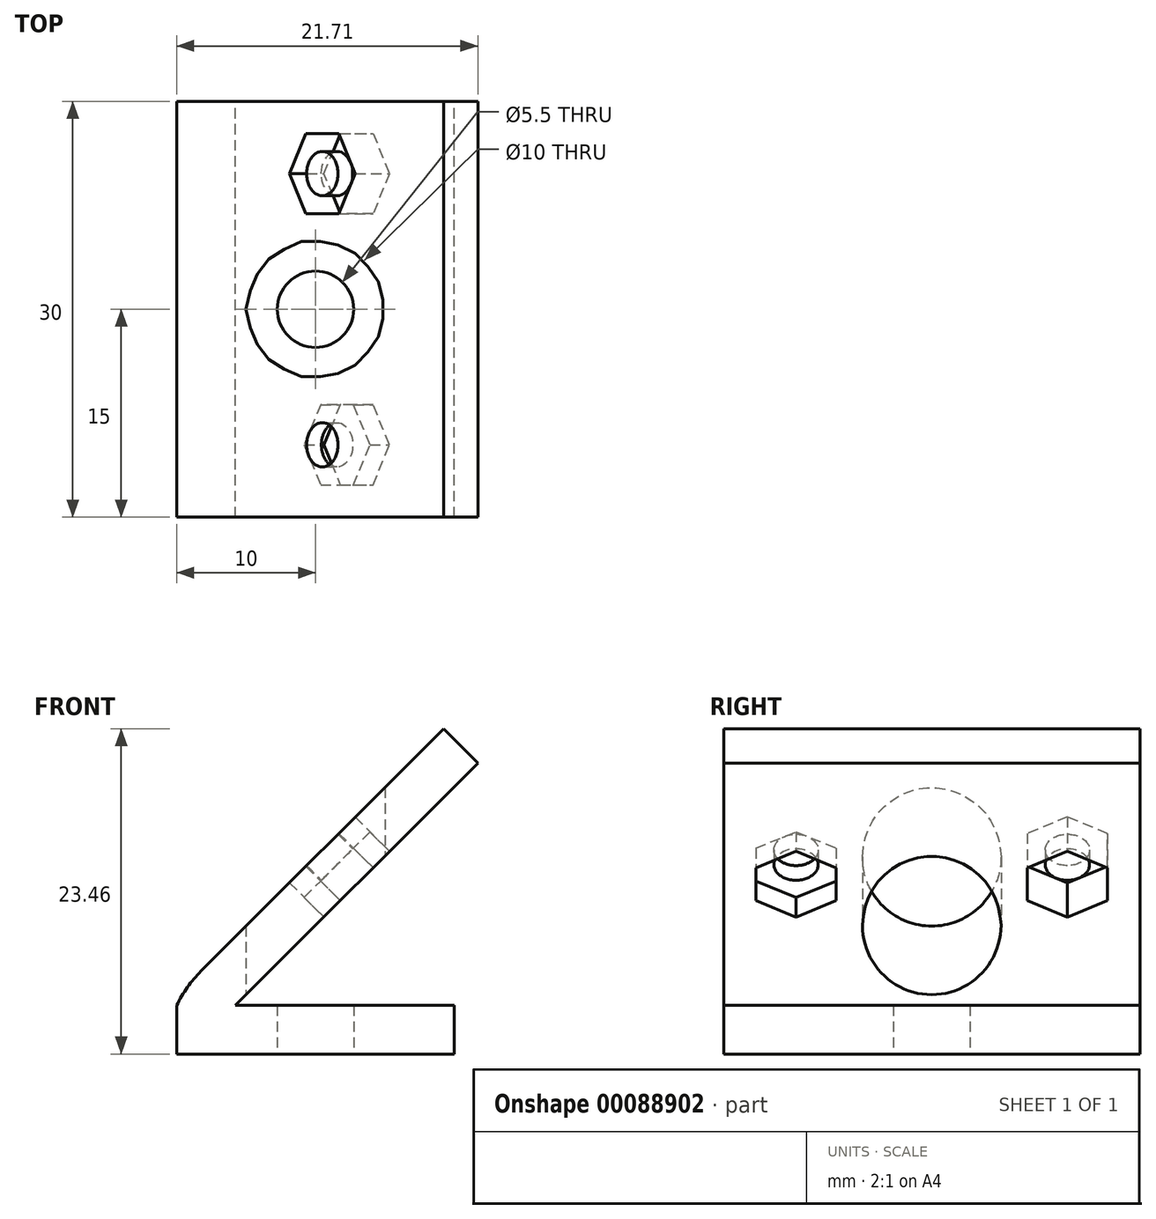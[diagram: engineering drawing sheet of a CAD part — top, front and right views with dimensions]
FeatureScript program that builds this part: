
annotation { "Feature Type Name" : "Feature", "Feature Type Description" : "" }
export const myFeature = defineFeature(function(context is Context, id is Id, definition is map)
    precondition{}
    {
        {
            var Q0;
            Q0=qCreatedBy(makeId("Front.planeOp"),FACE);
            var sketch = newSketch(context, id + "F0", { "sketchPlane" : qUnion([Q0])});
            skLineSegment(sketch, "E0.bottom", {"start": v(0, 0) * mm, "end": v(20, 0) * mm});
            skLineSegment(sketch, "E0.top", {"start": v(0, 3.5) * mm, "end": v(20, 3.5) * mm});
            skLineSegment(sketch, "E0.left", {"start": v(0, 0) * mm, "end": v(0, 3.5) * mm});
            skLineSegment(sketch, "E0.right", {"start": v(20, 0) * mm, "end": v(20, 3.5) * mm});
            skLineSegment(sketch, "E1", {"start": v(-13.12, -11.37) * mm, "end": v(33.48, 35.23) * mm, "construction": true});
            skPoint(sketch, "E2", {"position": v(0, 1.75) * mm});
            skLineSegment(sketch, "E3", {"start": v(-7.12, 1.75) * mm, "end": v(23.4, 1.75) * mm, "construction": true});
            skLineSegment(sketch, "E4", {"start": v(1.75, 5.97) * mm, "end": v(19.24, 23.46) * mm});
            skLineSegment(sketch, "E5", {"start": v(19.24, 23.46) * mm, "end": v(21.71, 20.99) * mm});
            skLineSegment(sketch, "E6", {"start": v(21.71, 20.99) * mm, "end": v(4.22, 3.5) * mm});
            skLineSegment(sketch, "E7", {"start": v(4.22, 3.5) * mm, "end": v(1.75, 5.97) * mm});
            skArc(sketch, "E8", {"start": v(1.75, 5.97) * mm, "mid": v(0.77, 4.81) * mm, "end": v(0, 3.5) * mm});
            skSolve(sketch);
        }
        {
            var Q0;
            Q0 = qSketchRegion(id + "F0", true);
            extrude(context, id + "F1", {"entities" : qUnion([Q0]), "depth" : 30 * mm});
        }
        {
            var Q0;
            Q0=makeQuery(id+"F1.opExtrude","SWEPT_FACE",FACE,{"disambiguationData":[OSD([sQuery(id+"F0.wireOp",EDGE,"E0.bottom")])]});
            var sketch = newSketch(context, id + "F2", { "sketchPlane" : qUnion([Q0])});
            skLineSegment(sketch, "E9", {"start": v(10, 34.29) * mm, "end": v(10, -9.4) * mm, "construction": true});
            skLineSegment(sketch, "E10", {"start": v(-12.53, 15) * mm, "end": v(35.25, 15) * mm, "construction": true});
            skCircle(sketch, "E11", {"center": v(10, 15) * mm, "radius": 2.75 * mm});
            skSolve(sketch);
        }
        {
            var Q0;
            Q0 = qSketchRegion(id + "F2", true);
            extrude(context, id + "F3", {"entities" : qUnion([Q0]), "operationType" : NewBodyOperationType.REMOVE, "endBound" : BoundingType.UP_TO_NEXT, "oppositeDirection" : true, "depth" : 25 * mm});
        }
        {
            var Q0;
            Q0=makeQuery(id+"F1.opExtrude","SWEPT_FACE",FACE,{"disambiguationData":[OSD([sQuery(id+"F0.wireOp",EDGE,"E0.top")])]});
            var sketch = newSketch(context, id + "F4", { "sketchPlane" : qUnion([Q0])});
            skCircle(sketch, "E12", {"center": v(10, -15) * mm, "radius": 5 * mm});
            skSolve(sketch);
        }
        {
            var Q0;
            Q0 = qSketchRegion(id + "F4", true);
            var Q1;
            Q1=makeQuery(id+"F1.opExtrude","SWEPT_FACE",FACE,{"disambiguationData":[OSD([sQuery(id+"F0.wireOp",EDGE,"E4")])]});
            extrude(context, id + "F5", {"entities" : qUnion([Q0]), "operationType" : NewBodyOperationType.REMOVE, "endBound" : BoundingType.UP_TO_SURFACE, "endBoundEntityFace" : qUnion([Q1]), "depth" : 25 * mm});
        }
        {
            var Q0;
            Q0=makeQuery(id+"F1.opExtrude","SWEPT_FACE",FACE,{"disambiguationData":[OSD([sQuery(id+"F0.wireOp",EDGE,"E6")])]});
            var sketch = newSketch(context, id + "F6", { "sketchPlane" : qUnion([Q0])});
            skLineSegment(sketch, "E13", {"start": v(-15, 41) * mm, "end": v(-15, -8.25) * mm, "construction": true});
            skCircle(sketch, "E14", {"center": v(-24.78, 17.83) * mm, "radius": 1.6 * mm});
            skCircle(sketch, "E15.MirrorC", {"center": v(-5.22, 17.83) * mm, "radius": 1.6 * mm});
            skLineSegment(sketch, "E16", {"start": v(22.15, 17.83) * mm, "end": v(-62.8, 17.83) * mm, "construction": true});
            skCircle(sketch, "E17.cCircle", {"center": v(-24.78, 17.83) * mm, "radius": 2.9 * mm, "construction": true});
            skLineSegment(sketch, "E17.0", {"start": v(-24.78, 21.18) * mm, "end": v(-21.88, 19.5) * mm});
            skLineSegment(sketch, "E17.1", {"start": v(-21.88, 19.5) * mm, "end": v(-21.88, 16.15) * mm});
            skLineSegment(sketch, "E17.2", {"start": v(-21.88, 16.15) * mm, "end": v(-24.78, 14.48) * mm});
            skLineSegment(sketch, "E17.3", {"start": v(-24.78, 14.48) * mm, "end": v(-27.68, 16.15) * mm});
            skLineSegment(sketch, "E17.4", {"start": v(-27.68, 16.15) * mm, "end": v(-27.68, 19.5) * mm});
            skLineSegment(sketch, "E17.5", {"start": v(-27.68, 19.5) * mm, "end": v(-24.78, 21.18) * mm});
            skPoint(sketch, "E17.0.midPoint", {"position": v(-23.33, 20.34) * mm});
            skLineSegment(sketch, "E18.MirrorCS", {"start": v(-5.22, 14.48) * mm, "end": v(-2.32, 16.15) * mm});
            skLineSegment(sketch, "E19.MirrorCS", {"start": v(-2.32, 16.15) * mm, "end": v(-2.32, 19.5) * mm});
            skLineSegment(sketch, "E20.MirrorCS", {"start": v(-2.32, 19.5) * mm, "end": v(-5.22, 21.18) * mm});
            skPoint(sketch, "E21.MirrorP", {"position": v(-6.67, 20.34) * mm});
            skCircle(sketch, "E22.MirrorC", {"center": v(-5.22, 17.83) * mm, "radius": 2.9 * mm, "construction": true});
            skLineSegment(sketch, "E23.MirrorCS", {"start": v(-8.12, 19.5) * mm, "end": v(-8.12, 16.15) * mm});
            skLineSegment(sketch, "E24.MirrorCS", {"start": v(-8.12, 16.15) * mm, "end": v(-5.22, 14.48) * mm});
            skLineSegment(sketch, "E25.MirrorCS", {"start": v(-5.22, 21.18) * mm, "end": v(-8.12, 19.5) * mm});
            skSolve(sketch);
        }
        {
            var Q0;
            Q0=makeQuery(id+"F6.imprint","IMPRINT",FACE,{"disambiguationData":[TD([[makeQuery(id+"F6.imprint","IMPRINT",EDGE,{"derivedFrom":sQuery(id+"F6.wireOp",EDGE,"E15.MirrorC")}),-1.0]])]});
            var Q1;
            Q1=makeQuery(id+"F6.imprint","IMPRINT",FACE,{"disambiguationData":[TD([[makeQuery(id+"F6.imprint","IMPRINT",EDGE,{"derivedFrom":sQuery(id+"F6.wireOp",EDGE,"E14")}),1.0]])]});
            extrude(context, id + "F7", {"entities" : qUnion([Q0, Q1]), "operationType" : NewBodyOperationType.REMOVE, "endBound" : BoundingType.UP_TO_NEXT, "oppositeDirection" : true, "depth" : 25 * mm});
        }
        {
            var Q0;
            Q0=makeQuery(id+"F6.imprint","IMPRINT",FACE,{"disambiguationData":[TD([[makeQuery(id+"F6.imprint","IMPRINT",EDGE,{"derivedFrom":sQuery(id+"F6.wireOp",EDGE,"E14")}),-1.0]])]});
            var Q1;
            Q1=makeQuery(id+"F6.imprint","IMPRINT",FACE,{"disambiguationData":[TD([[makeQuery(id+"F6.imprint","IMPRINT",EDGE,{"derivedFrom":sQuery(id+"F6.wireOp",EDGE,"E15.MirrorC")}),1.0]])]});
            extrude(context, id + "F8", {"entities" : qUnion([Q0, Q1]), "operationType" : NewBodyOperationType.REMOVE, "oppositeDirection" : true, "depth" : 2 * mm});
        }
    });
